# Revit family: Sink-Pedestal-KOHLER-Folio-K-2019X_1
name_source: partatom
category: Specialty Equipment
revit_build: Autodesk Revit 2017 (Build: 20160225_1515(x64)
units: mm (PartAtom-declared; Revit-internal decimal feet)

## family parameters
Cut with Voids When Loaded = No
Host = Face
OmniClass Number = 23.31.25.00
OmniClass Title = Toilet and Bath Specialties
Part Type = Normal
Room Calculation Point = No
Round Connector Dimension = Use Diameter
Shared = No

## types (1)
- 0-White
    ADA Compliant = No
    Assembly Code = C1030200
    Date Modified = 08/10/2020
    Default Elevation = 0"
    Description = Pedestal Only
    Finish = Kohler-Vitreous_China-0-White
    Height = 27"
    Length = 7 1/8"
    Manufacturer = KOHLER Co.
    Master Format 2014 = 10 28 00
    Master Format 2014 Name = Toilet, Bath, and Laundry Accessories
    Material = Vitreous China
    Model = K-2019X-0
    Product Documentation Link = http://resources.kohler.com
    Product Name = Folio
    Product Page URL = https://www.kohler.co.th
    Type = 1
    URL = https://www.kohler.co.th
    WaterSense Certified = No
    Width = 6 3/4"

## geometry (parser evidence)
native form markers: Sweep x6
no freeform markers — native parametric forms only
